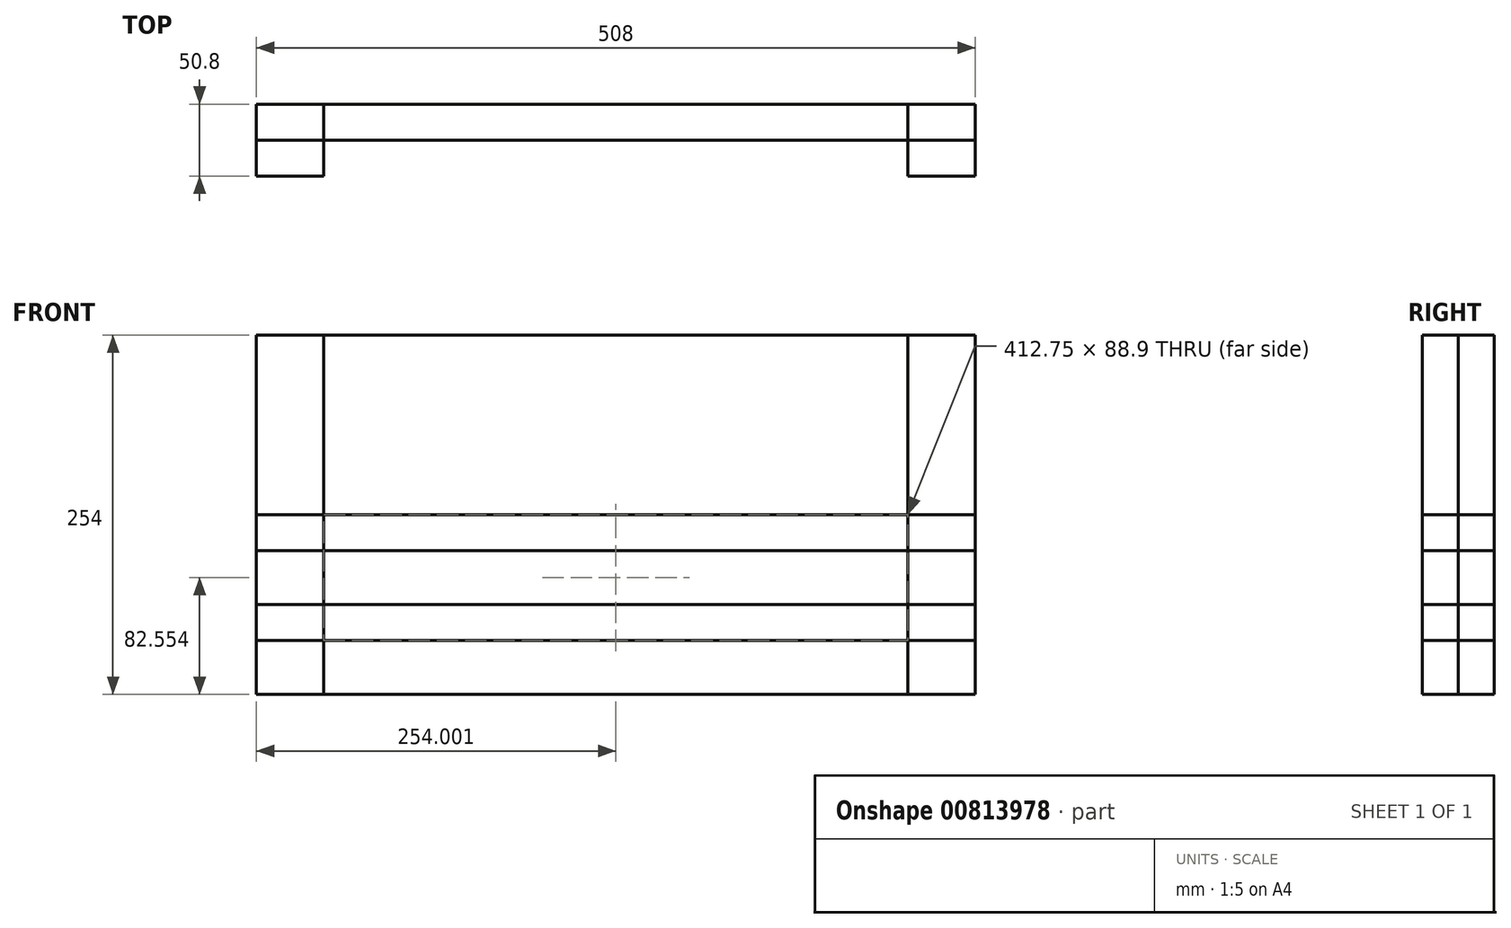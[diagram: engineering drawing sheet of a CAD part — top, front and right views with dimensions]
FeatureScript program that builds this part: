
annotation { "Feature Type Name" : "Feature", "Feature Type Description" : "" }
export const myFeature = defineFeature(function(context is Context, id is Id, definition is map)
    precondition{}
    {
        {
            var Q0;
            Q0=qCreatedBy(makeId("Front.planeOp"),FACE);
            var sketch = newSketch(context, id + "F0", { "sketchPlane" : qUnion([Q0])});
            skLineSegment(sketch, "E0.bottom", {"start": v(-265.67, 138.42) * mm, "end": v(242.33, 138.42) * mm});
            skLineSegment(sketch, "E0.top", {"start": v(-265.67, -115.58) * mm, "end": v(242.33, -115.58) * mm});
            skLineSegment(sketch, "E0.left", {"start": v(-265.67, 138.42) * mm, "end": v(-265.67, -115.58) * mm});
            skLineSegment(sketch, "E0.right", {"start": v(242.33, 138.42) * mm, "end": v(242.33, -115.58) * mm});
            skLineSegment(sketch, "E1.bottom", {"start": v(-265.67, 138.42) * mm, "end": v(-218.04, 138.42) * mm});
            skLineSegment(sketch, "E1.top", {"start": v(-265.67, -115.58) * mm, "end": v(-218.04, -115.58) * mm});
            skLineSegment(sketch, "E1.right", {"start": v(-218.04, 138.42) * mm, "end": v(-218.04, -115.58) * mm});
            skLineSegment(sketch, "E2.bottom", {"start": v(194.7, 138.42) * mm, "end": v(242.33, 138.42) * mm});
            skLineSegment(sketch, "E2.top", {"start": v(194.7, -115.58) * mm, "end": v(242.33, -115.58) * mm});
            skLineSegment(sketch, "E2.left", {"start": v(194.7, 138.42) * mm, "end": v(194.7, -115.58) * mm});
            skLineSegment(sketch, "E3.bottom", {"start": v(-265.67, -77.48) * mm, "end": v(242.33, -77.48) * mm});
            skLineSegment(sketch, "E3.top", {"start": v(-265.67, -52.08) * mm, "end": v(242.33, -52.08) * mm});
            skLineSegment(sketch, "E3.left", {"start": v(-265.67, -77.48) * mm, "end": v(-265.67, -52.08) * mm});
            skLineSegment(sketch, "E3.right", {"start": v(242.33, -77.48) * mm, "end": v(242.33, -52.08) * mm});
            skLineSegment(sketch, "E4.bottom", {"start": v(-265.67, -13.98) * mm, "end": v(242.33, -13.98) * mm});
            skLineSegment(sketch, "E4.top", {"start": v(-265.67, 11.42) * mm, "end": v(242.33, 11.42) * mm});
            skLineSegment(sketch, "E4.left", {"start": v(-265.67, -13.98) * mm, "end": v(-265.67, 11.42) * mm});
            skLineSegment(sketch, "E4.right", {"start": v(242.33, -13.98) * mm, "end": v(242.33, 11.42) * mm});
            skSolve(sketch);
        }
        {
            var Q0;
            {var subQ0=sQuery(id+"F0.wireOp",EDGE,"E1.right");var subQ1=sQuery(id+"F0.wireOp",EDGE,"E0.top");var subQ2=makeQuery(id+"F0.imprint","INTERSECT",VERTEX,{"derivedFrom":[subQ1,subQ0]});var subQ3=sQuery(id+"F0.wireOp",EDGE,"E0.left");var subQ5=sQuery(id+"F0.wireOp",EDGE,"E3.bottom");var subQ10=sQuery(id+"F0.wireOp",EDGE,"E4.bottom");var subQ11=makeQuery(id+"F0.imprint","INTERSECT",VERTEX,{"derivedFrom":[subQ3,subQ10]});var subQ22=sQuery(id+"F0.wireOp",EDGE,"E0.bottom");var subQ23=makeQuery(id+"F0.imprint","INTERSECT",VERTEX,{"derivedFrom":[subQ22,subQ0]});var subQ26=sQuery(id+"F0.wireOp",EDGE,"E0.right");var subQ27=makeQuery(id+"F0.imprint","INTERSECT",VERTEX,{"derivedFrom":[subQ26,subQ10]});var subQ33=sQuery(id+"F0.wireOp",EDGE,"E3.top");var subQ34=makeQuery(id+"F0.imprint","INTERSECT",VERTEX,{"derivedFrom":[subQ3,subQ33]});var subQ39=makeQuery(id+"F0.imprint","INTERSECT",VERTEX,{"derivedFrom":[subQ22,subQ26]});var subQ40=makeQuery(id+"F0.imprint","INTERSECT",VERTEX,{"derivedFrom":[subQ26,subQ5]});var subQ45=makeQuery(id+"F0.imprint","INTERSECT",VERTEX,{"derivedFrom":[subQ1,subQ26]});Q0=qUnion([makeQuery(id+"F0.imprint","IMPRINT",FACE,{"disambiguationData":[TD([[makeQuery(id+"F0.imprint","IMPRINT",EDGE,{"disambiguationData":[TD([[subQ27,-1.0]])],"derivedFrom":subQ26}),-1.0]])]}),makeQuery(id+"F0.imprint","IMPRINT",FACE,{"disambiguationData":[TD([[makeQuery(id+"F0.imprint","IMPRINT",EDGE,{"disambiguationData":[TD([[subQ45,1.0]])],"derivedFrom":subQ1}),1.0]])]}),makeQuery(id+"F0.imprint","IMPRINT",FACE,{"disambiguationData":[TD([[makeQuery(id+"F0.imprint","IMPRINT",EDGE,{"disambiguationData":[TD([[subQ11,-1.0]])],"derivedFrom":subQ3}),1.0]])]}),makeQuery(id+"F0.imprint","IMPRINT",FACE,{"disambiguationData":[TD([[makeQuery(id+"F0.imprint","IMPRINT",EDGE,{"disambiguationData":[TD([[subQ40,1.0]])],"derivedFrom":subQ26}),-1.0]])]}),makeQuery(id+"F0.imprint","IMPRINT",FACE,{"disambiguationData":[TD([[makeQuery(id+"F0.imprint","IMPRINT",EDGE,{"disambiguationData":[TD([[subQ39,1.0]])],"derivedFrom":subQ22}),-1.0]])]}),makeQuery(id+"F0.imprint","IMPRINT",FACE,{"disambiguationData":[TD([[makeQuery(id+"F0.imprint","IMPRINT",EDGE,{"disambiguationData":[TD([[subQ23,-1.0]])],"derivedFrom":subQ22}),-1.0]])]}),makeQuery(id+"F0.imprint","IMPRINT",FACE,{"disambiguationData":[TD([[makeQuery(id+"F0.imprint","IMPRINT",EDGE,{"disambiguationData":[TD([[subQ34,-1.0]])],"derivedFrom":subQ3}),1.0]])]}),makeQuery(id+"F0.imprint","IMPRINT",FACE,{"disambiguationData":[TD([[makeQuery(id+"F0.imprint","IMPRINT",EDGE,{"disambiguationData":[TD([[subQ27,1.0]])],"derivedFrom":subQ26}),-1.0]])]}),makeQuery(id+"F0.imprint","IMPRINT",FACE,{"disambiguationData":[TD([[makeQuery(id+"F0.imprint","IMPRINT",EDGE,{"disambiguationData":[TD([[subQ23,1.0]])],"derivedFrom":subQ22}),-1.0]])]}),makeQuery(id+"F0.imprint","IMPRINT",FACE,{"disambiguationData":[TD([[makeQuery(id+"F0.imprint","IMPRINT",EDGE,{"disambiguationData":[TD([[subQ2,-1.0]])],"derivedFrom":subQ1}),1.0]])]}),makeQuery(id+"F0.imprint","IMPRINT",FACE,{"disambiguationData":[TD([[makeQuery(id+"F0.imprint","IMPRINT",EDGE,{"disambiguationData":[TD([[subQ11,1.0]])],"derivedFrom":subQ3}),1.0]])]}),makeQuery(id+"F0.imprint","IMPRINT",FACE,{"disambiguationData":[TD([[makeQuery(id+"F0.imprint","IMPRINT",EDGE,{"disambiguationData":[TD([[subQ2,1.0]])],"derivedFrom":subQ1}),1.0]])]})]);}
            extrude(context, id + "F1", {"entities" : qUnion([Q0]), "depth" : 25.4 * mm, "offsetDistance" : 25.4 * mm});
        }
        {
            var Q0;
            {var subQ0=sQuery(id+"F0.wireOp",EDGE,"E1.right");var subQ1=sQuery(id+"F0.wireOp",EDGE,"E0.bottom");var subQ2=makeQuery(id+"F0.imprint","INTERSECT",VERTEX,{"derivedFrom":[subQ1,subQ0]});Q0=makeQuery(id+"F0.imprint","IMPRINT",FACE,{"disambiguationData":[TD([[makeQuery(id+"F0.imprint","IMPRINT",EDGE,{"disambiguationData":[TD([[subQ2,1.0]])],"derivedFrom":subQ1}),-1.0]])]});}
            extrude(context, id + "F2", {"entities" : qUnion([Q0]), "depth" : 50.8 * mm, "offsetDistance" : 25.4 * mm});
        }
        {
            var Q0;
            {var subQ0=sQuery(id+"F0.wireOp",EDGE,"E0.right");var subQ1=sQuery(id+"F0.wireOp",EDGE,"E0.bottom");var subQ2=makeQuery(id+"F0.imprint","INTERSECT",VERTEX,{"derivedFrom":[subQ1,subQ0]});Q0=makeQuery(id+"F0.imprint","IMPRINT",FACE,{"disambiguationData":[TD([[makeQuery(id+"F0.imprint","IMPRINT",EDGE,{"disambiguationData":[TD([[subQ2,1.0]])],"derivedFrom":subQ1}),-1.0]])]});}
            extrude(context, id + "F3", {"entities" : qUnion([Q0]), "depth" : 50.8 * mm, "offsetDistance" : 25.4 * mm});
        }
        {
            var Q0;
            {var subQ0=sQuery(id+"F0.wireOp",EDGE,"E3.top");var subQ1=sQuery(id+"F0.wireOp",EDGE,"E0.left");var subQ2=makeQuery(id+"F0.imprint","INTERSECT",VERTEX,{"derivedFrom":[subQ1,subQ0]});Q0=makeQuery(id+"F0.imprint","IMPRINT",FACE,{"disambiguationData":[TD([[makeQuery(id+"F0.imprint","IMPRINT",EDGE,{"disambiguationData":[TD([[subQ2,-1.0]])],"derivedFrom":subQ1}),1.0]])]});}
            var Q1;
            {var subQ0=sQuery(id+"F0.wireOp",EDGE,"E3.bottom");var subQ1=sQuery(id+"F0.wireOp",EDGE,"E0.right");var subQ2=makeQuery(id+"F0.imprint","INTERSECT",VERTEX,{"derivedFrom":[subQ1,subQ0]});Q1=makeQuery(id+"F0.imprint","IMPRINT",FACE,{"disambiguationData":[TD([[makeQuery(id+"F0.imprint","IMPRINT",EDGE,{"disambiguationData":[TD([[subQ2,1.0]])],"derivedFrom":subQ1}),-1.0]])]});}
            extrude(context, id + "F4", {"entities" : qUnion([Q0, Q1]), "depth" : 50.8 * mm, "offsetDistance" : 25.4 * mm});
        }
        {
            var Q0;
            {var subQ0=sQuery(id+"F0.wireOp",EDGE,"E3.bottom");var subQ1=sQuery(id+"F0.wireOp",EDGE,"E1.right");var subQ2=makeQuery(id+"F0.imprint","INTERSECT",VERTEX,{"derivedFrom":[subQ1,subQ0]});Q0=makeQuery(id+"F0.imprint","IMPRINT",FACE,{"disambiguationData":[TD([[makeQuery(id+"F0.imprint","IMPRINT",EDGE,{"disambiguationData":[TD([[subQ2,1.0]])],"derivedFrom":subQ1}),1.0]])]});}
            extrude(context, id + "F5", {"entities" : qUnion([Q0]), "depth" : 25.4 * mm, "offsetDistance" : 25.4 * mm});
        }
        {
            var Q0;
            {var subQ0=sQuery(id+"F0.wireOp",EDGE,"E1.right");var subQ1=sQuery(id+"F0.wireOp",EDGE,"E0.top");var subQ2=makeQuery(id+"F0.imprint","INTERSECT",VERTEX,{"derivedFrom":[subQ1,subQ0]});Q0=makeQuery(id+"F0.imprint","IMPRINT",FACE,{"disambiguationData":[TD([[makeQuery(id+"F0.imprint","IMPRINT",EDGE,{"disambiguationData":[TD([[subQ2,1.0]])],"derivedFrom":subQ1}),1.0]])]});}
            var Q1;
            {var subQ0=sQuery(id+"F0.wireOp",EDGE,"E0.right");var subQ1=sQuery(id+"F0.wireOp",EDGE,"E0.top");var subQ2=makeQuery(id+"F0.imprint","INTERSECT",VERTEX,{"derivedFrom":[subQ1,subQ0]});Q1=makeQuery(id+"F0.imprint","IMPRINT",FACE,{"disambiguationData":[TD([[makeQuery(id+"F0.imprint","IMPRINT",EDGE,{"disambiguationData":[TD([[subQ2,1.0]])],"derivedFrom":subQ1}),1.0]])]});}
            extrude(context, id + "F6", {"entities" : qUnion([Q0, Q1]), "depth" : 50.8 * mm, "offsetDistance" : 25.4 * mm});
        }
        {
            var Q0;
            {var subQ0=sQuery(id+"F0.wireOp",EDGE,"E4.bottom");var subQ1=sQuery(id+"F0.wireOp",EDGE,"E0.left");var subQ2=makeQuery(id+"F0.imprint","INTERSECT",VERTEX,{"derivedFrom":[subQ1,subQ0]});Q0=makeQuery(id+"F0.imprint","IMPRINT",FACE,{"disambiguationData":[TD([[makeQuery(id+"F0.imprint","IMPRINT",EDGE,{"disambiguationData":[TD([[subQ2,1.0]])],"derivedFrom":subQ1}),1.0]])]});}
            var Q1;
            {var subQ0=sQuery(id+"F0.wireOp",EDGE,"E4.bottom");var subQ1=sQuery(id+"F0.wireOp",EDGE,"E0.right");var subQ2=makeQuery(id+"F0.imprint","INTERSECT",VERTEX,{"derivedFrom":[subQ1,subQ0]});Q1=makeQuery(id+"F0.imprint","IMPRINT",FACE,{"disambiguationData":[TD([[makeQuery(id+"F0.imprint","IMPRINT",EDGE,{"disambiguationData":[TD([[subQ2,1.0]])],"derivedFrom":subQ1}),-1.0]])]});}
            extrude(context, id + "F7", {"entities" : qUnion([Q0, Q1]), "depth" : 50.8 * mm, "offsetDistance" : 25.4 * mm});
        }
        {
            var Q0;
            {var subQ0=sQuery(id+"F0.wireOp",EDGE,"E4.bottom");var subQ1=sQuery(id+"F0.wireOp",EDGE,"E1.right");var subQ2=makeQuery(id+"F0.imprint","INTERSECT",VERTEX,{"derivedFrom":[subQ1,subQ0]});Q0=makeQuery(id+"F0.imprint","IMPRINT",FACE,{"disambiguationData":[TD([[makeQuery(id+"F0.imprint","IMPRINT",EDGE,{"disambiguationData":[TD([[subQ2,1.0]])],"derivedFrom":subQ1}),1.0]])]});}
            extrude(context, id + "F8", {"entities" : qUnion([Q0]), "depth" : 25.4 * mm, "offsetDistance" : 25.4 * mm});
        }
        {
            var Q0;
            {var subQ0=sQuery(id+"F0.wireOp",EDGE,"E4.bottom");var subQ1=sQuery(id+"F0.wireOp",EDGE,"E0.left");var subQ2=makeQuery(id+"F0.imprint","INTERSECT",VERTEX,{"derivedFrom":[subQ1,subQ0]});Q0=makeQuery(id+"F0.imprint","IMPRINT",FACE,{"disambiguationData":[TD([[makeQuery(id+"F0.imprint","IMPRINT",EDGE,{"disambiguationData":[TD([[subQ2,-1.0]])],"derivedFrom":subQ1}),1.0]])]});}
            var Q1;
            {var subQ0=sQuery(id+"F0.wireOp",EDGE,"E4.bottom");var subQ1=sQuery(id+"F0.wireOp",EDGE,"E0.right");var subQ2=makeQuery(id+"F0.imprint","INTERSECT",VERTEX,{"derivedFrom":[subQ1,subQ0]});Q1=makeQuery(id+"F0.imprint","IMPRINT",FACE,{"disambiguationData":[TD([[makeQuery(id+"F0.imprint","IMPRINT",EDGE,{"disambiguationData":[TD([[subQ2,-1.0]])],"derivedFrom":subQ1}),-1.0]])]});}
            extrude(context, id + "F9", {"entities" : qUnion([Q0, Q1]), "depth" : 50.8 * mm, "offsetDistance" : 25.4 * mm});
        }
        {
            var Q0;
            {var subQ0=sQuery(id+"F0.wireOp",EDGE,"E4.bottom");var subQ1=sQuery(id+"F0.wireOp",EDGE,"E1.right");var subQ2=makeQuery(id+"F0.imprint","INTERSECT",VERTEX,{"derivedFrom":[subQ1,subQ0]});Q0=makeQuery(id+"F0.imprint","IMPRINT",FACE,{"disambiguationData":[TD([[makeQuery(id+"F0.imprint","IMPRINT",EDGE,{"disambiguationData":[TD([[subQ2,-1.0]])],"derivedFrom":subQ1}),1.0]])]});}
            extrude(context, id + "F10", {"entities" : qUnion([Q0]), "depth" : 25.4 * mm, "offsetDistance" : 25.4 * mm});
        }
    });
